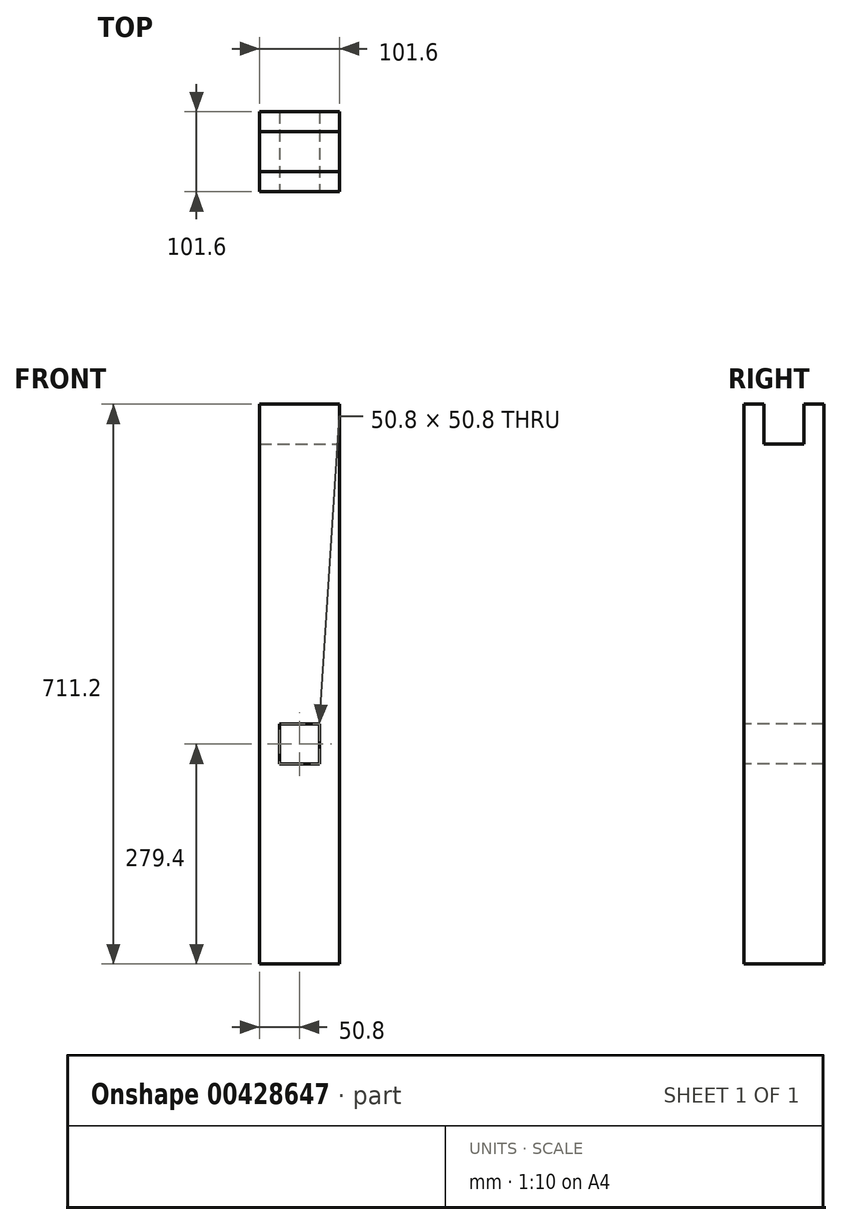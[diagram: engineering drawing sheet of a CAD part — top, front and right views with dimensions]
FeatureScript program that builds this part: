
annotation { "Feature Type Name" : "Feature", "Feature Type Description" : "" }
export const myFeature = defineFeature(function(context is Context, id is Id, definition is map)
    precondition{}
    {
        {
            var Q0;
            Q0=qCreatedBy(makeId("Front.planeOp"),FACE);
            var sketch = newSketch(context, id + "F0", { "sketchPlane" : qUnion([Q0])});
            skLineSegment(sketch, "E0.bottom", {"start": v(-50.8, 355.6) * mm, "end": v(50.8, 355.6) * mm});
            skLineSegment(sketch, "E0.top", {"start": v(-50.8, -355.6) * mm, "end": v(50.8, -355.6) * mm});
            skLineSegment(sketch, "E0.left", {"start": v(-50.8, 355.6) * mm, "end": v(-50.8, -355.6) * mm});
            skLineSegment(sketch, "E0.right", {"start": v(50.8, 355.6) * mm, "end": v(50.8, -355.6) * mm});
            skPoint(sketch, "E0.middle", {"position": v(0, 0) * mm});
            skSolve(sketch);
        }
        {
            var Q0;
            Q0 = qSketchRegion(id + "F0", true);
            extrude(context, id + "F1", {"entities" : qUnion([Q0]), "depth" : 101.6 * mm});
        }
        {
            var Q0;
            Q0=makeQuery(id+"F1.opExtrude","SWEPT_FACE",FACE,{"disambiguationData":[OSD([sQuery(id+"F0.wireOp",EDGE,"E0.bottom")])]});
            var sketch = newSketch(context, id + "F2", { "sketchPlane" : qUnion([Q0])});
            skPoint(sketch, "E1.endSnap0", {"position": v(0, 0) * mm});
            skPoint(sketch, "E2.endSnap0", {"position": v(0, -101.6) * mm});
            skLineSegment(sketch, "E3.bottom", {"start": v(-50.8, -25.4) * mm, "end": v(50.8, -25.4) * mm});
            skLineSegment(sketch, "E3.top", {"start": v(-50.8, -76.2) * mm, "end": v(50.8, -76.2) * mm});
            skLineSegment(sketch, "E3.left", {"start": v(-50.8, -25.4) * mm, "end": v(-50.8, -76.2) * mm});
            skLineSegment(sketch, "E3.right", {"start": v(50.8, -25.4) * mm, "end": v(50.8, -76.2) * mm});
            skSolve(sketch);
        }
        {
            var Q0;
            Q0 = qSketchRegion(id + "F2", true);
            extrude(context, id + "F3", {"entities" : qUnion([Q0]), "operationType" : NewBodyOperationType.REMOVE, "oppositeDirection" : true, "depth" : 50.8 * mm});
        }
        {
            var Q0;
            Q0=makeQuery(id+"F1.opExtrude","CAP_FACE",FACE,{"disambiguationData":[OSD([sQuery(id+"F0.wireOp",EDGE,"E0.bottom"),sQuery(id+"F0.wireOp",EDGE,"E0.top"),sQuery(id+"F0.wireOp",EDGE,"E0.left"),sQuery(id+"F0.wireOp",EDGE,"E0.right")])],"isStart":false});
            var sketch = newSketch(context, id + "F4", { "sketchPlane" : qUnion([Q0])});
            skLineSegment(sketch, "E4", {"start": v(0, -355.6) * mm, "end": v(0, -101.6) * mm});
            skPoint(sketch, "E4.endSnap0", {"position": v(0, -355.6) * mm});
            skLineSegment(sketch, "E5.bottom", {"start": v(25.4, -101.6) * mm, "end": v(-25.4, -101.6) * mm});
            skLineSegment(sketch, "E5.top", {"start": v(25.4, -50.8) * mm, "end": v(-25.4, -50.8) * mm});
            skLineSegment(sketch, "E5.left", {"start": v(25.4, -101.6) * mm, "end": v(25.4, -50.8) * mm});
            skLineSegment(sketch, "E5.right", {"start": v(-25.4, -101.6) * mm, "end": v(-25.4, -50.8) * mm});
            skSolve(sketch);
        }
        {
            var Q0;
            Q0 = qSketchRegion(id + "F4", true);
            extrude(context, id + "F5", {"entities" : qUnion([Q0]), "operationType" : NewBodyOperationType.REMOVE, "oppositeDirection" : true, "depth" : 101.6 * mm});
        }
    });
